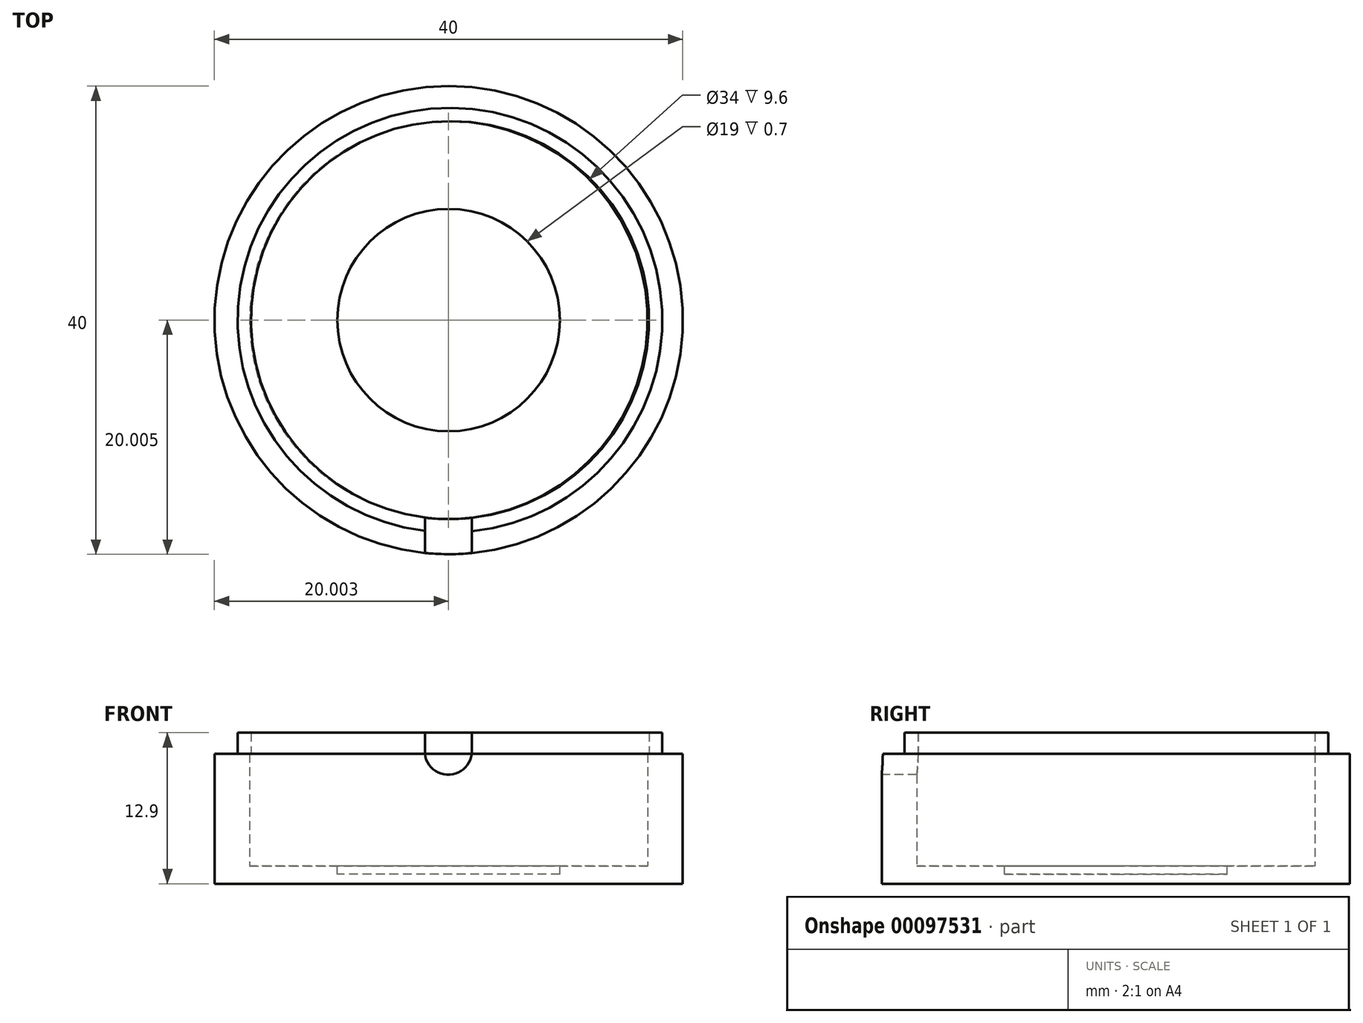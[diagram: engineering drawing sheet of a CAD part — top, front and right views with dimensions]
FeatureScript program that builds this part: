
annotation { "Feature Type Name" : "Feature", "Feature Type Description" : "" }
export const myFeature = defineFeature(function(context is Context, id is Id, definition is map)
    precondition{}
    {
        {
            var Q0;
            Q0=qCreatedBy(makeId("Top.planeOp"),FACE);
            var sketch = newSketch(context, id + "F0", { "sketchPlane" : qUnion([Q0])});
            skCircle(sketch, "E0", {"center": v(-50.79, 33.4) * mm, "radius": 20 * mm});
            skSolve(sketch);
        }
        {
            var Q0;
            Q0=makeQuery(id+"F0.imprint","IMPRINT",FACE,{"disambiguationData":[TD([[makeQuery(id+"F0.imprint","IMPRINT",EDGE,{"derivedFrom":sQuery(id+"F0.wireOp",EDGE,"E0")}),1.0]])]});
            extrude(context, id + "F1", {"entities" : qUnion([Q0]), "depth" : 1.5 * mm});
        }
        {
            var Q0;
            Q0=makeQuery(id+"F1.opExtrude","CAP_FACE",FACE,{"disambiguationData":[OSD([sQuery(id+"F0.wireOp",EDGE,"E0"),sQuery(id+"F0.wireOp",EDGE,"IqYGBItP-6JEx-q2S6-xiGm-nLTTzCfwcT9q")])],"isStart":false});
            var sketch = newSketch(context, id + "F2", { "sketchPlane" : qUnion([Q0])});
            skCircle(sketch, "E1", {"center": v(-50.79, 33.4) * mm, "radius": 17 * mm});
            skSolve(sketch);
        }
        {
            var Q0;
            Q0=makeQuery(id+"F2.imprint","IMPRINT",FACE,{"disambiguationData":[TD([[makeQuery(id+"F2.imprint","IMPRINT",EDGE,{"derivedFrom":sQuery(id+"F2.wireOp",EDGE,"E1")}),-1.0]])]});
            extrude(context, id + "F3", {"entities" : qUnion([Q0]), "operationType" : NewBodyOperationType.ADD, "depth" : 9.6 * mm});
        }
        {
            var Q0;
            Q0=makeQuery(id+"F3.opExtrude","CAP_FACE",FACE,{"disambiguationData":[OSD([sQuery(id+"F0.wireOp",EDGE,"E0"),sQuery(id+"F2.wireOp",EDGE,"E1")])],"isStart":false});
            var sketch = newSketch(context, id + "F4", { "sketchPlane" : qUnion([Q0])});
            skLineSegment(sketch, "E2", {"start": v(-50.67, 50.4) * mm, "end": v(-50.67, 16.4) * mm, "construction": true});
            skCircle(sketch, "E3", {"center": v(-50.67, 33.4) * mm, "radius": 18.14 * mm});
            skLineSegment(sketch, "E4", {"start": v(-50.67, 33.4) * mm, "end": v(-25.06, 33.4) * mm, "construction": true});
            skLineSegment(sketch, "E5", {"start": v(-33.79, 33.4) * mm, "end": v(-32.54, 33.4) * mm, "construction": true});
            skCircle(sketch, "E6", {"center": v(-50.67, 33.4) * mm, "radius": 17 * mm});
            skSolve(sketch);
        }
        {
            var Q0;
            Q0 = qSketchRegion(id + "F4", true);
            extrude(context, id + "F5", {"entities" : qUnion([Q0]), "operationType" : NewBodyOperationType.ADD, "depth" : 1.8 * mm});
        }
        {
            var Q0;
            Q0=qCreatedBy(makeId("Front.planeOp"),FACE);
            var sketch = newSketch(context, id + "F6", { "sketchPlane" : qUnion([Q0])});
            skLineSegment(sketch, "E7", {"start": v(-70.82, 9.31) * mm, "end": v(-30.82, 9.31) * mm, "construction": true});
            skLineSegment(sketch, "E8", {"start": v(-30.82, 11.11) * mm, "end": v(-30.82, 8.32) * mm, "construction": true});
            skLineSegment(sketch, "E9", {"start": v(-70.82, 9.44) * mm, "end": v(-70.82, 9.24) * mm, "construction": true});
            skPoint(sketch, "E10.end.orphan", {"position": v(-50.83, 0) * mm});
            skLineSegment(sketch, "E11", {"start": v(-50.82, 9.31) * mm, "end": v(-50.82, 17.42) * mm, "construction": true});
            skLineSegment(sketch, "E12", {"start": v(-52.82, 17.42) * mm, "end": v(-52.82, 11.1) * mm});
            skLineSegment(sketch, "E13.MirrorCS", {"start": v(-48.82, 17.42) * mm, "end": v(-48.82, 11.1) * mm});
            skArc(sketch, "E14", {"start": v(-52.82, 11.1) * mm, "mid": v(-50.82, 9.31) * mm, "end": v(-48.82, 11.1) * mm});
            skLineSegment(sketch, "E15", {"start": v(-52.82, 17.42) * mm, "end": v(-48.82, 17.42) * mm});
            skSolve(sketch);
        }
        {
            var Q0;
            Q0=makeQuery(id+"F6.imprint","IMPRINT",FACE,{"disambiguationData":[TD([[makeQuery(id+"F6.imprint","IMPRINT",EDGE,{"derivedFrom":sQuery(id+"F6.wireOp",EDGE,"E12")}),1.0]])]});
            var Q1;
            Q1=sQuery(id+"F6.wireOp",EDGE,"E15");
            var Q2;
            Q2=sQuery(id+"F6.wireOp",EDGE,"E12");
            var Q3;
            Q3=sQuery(id+"F6.wireOp",EDGE,"E13.MirrorCS");
            var Q4;
            Q4=sQuery(id+"F6.wireOp",EDGE,"E14");
            extrude(context, id + "F7", {"entities" : qUnion([Q0]), "operationType" : NewBodyOperationType.REMOVE, "surfaceEntities" : qUnion([Q1, Q2, Q3, Q4]), "oppositeDirection" : true, "depth" : 20 * mm});
        }
        {
            var Q0;
            Q0=makeQuery(id+"F1.opExtrude","CAP_FACE",FACE,{"disambiguationData":[OSD([sQuery(id+"F0.wireOp",EDGE,"E0")])],"isStart":false});
            var sketch = newSketch(context, id + "F8", { "sketchPlane" : qUnion([Q0])});
            skCircle(sketch, "E16", {"center": v(-50.79, 33.4) * mm, "radius": 9.5 * mm});
            skSolve(sketch);
        }
        {
            var Q0;
            Q0=makeQuery(id+"F8.imprint","IMPRINT",FACE,{"disambiguationData":[TD([[makeQuery(id+"F8.imprint","IMPRINT",EDGE,{"derivedFrom":sQuery(id+"F8.wireOp",EDGE,"E16")}),1.0]])]});
            extrude(context, id + "F9", {"entities" : qUnion([Q0]), "operationType" : NewBodyOperationType.REMOVE, "oppositeDirection" : true, "depth" : 0.7 * mm});
        }
    });
